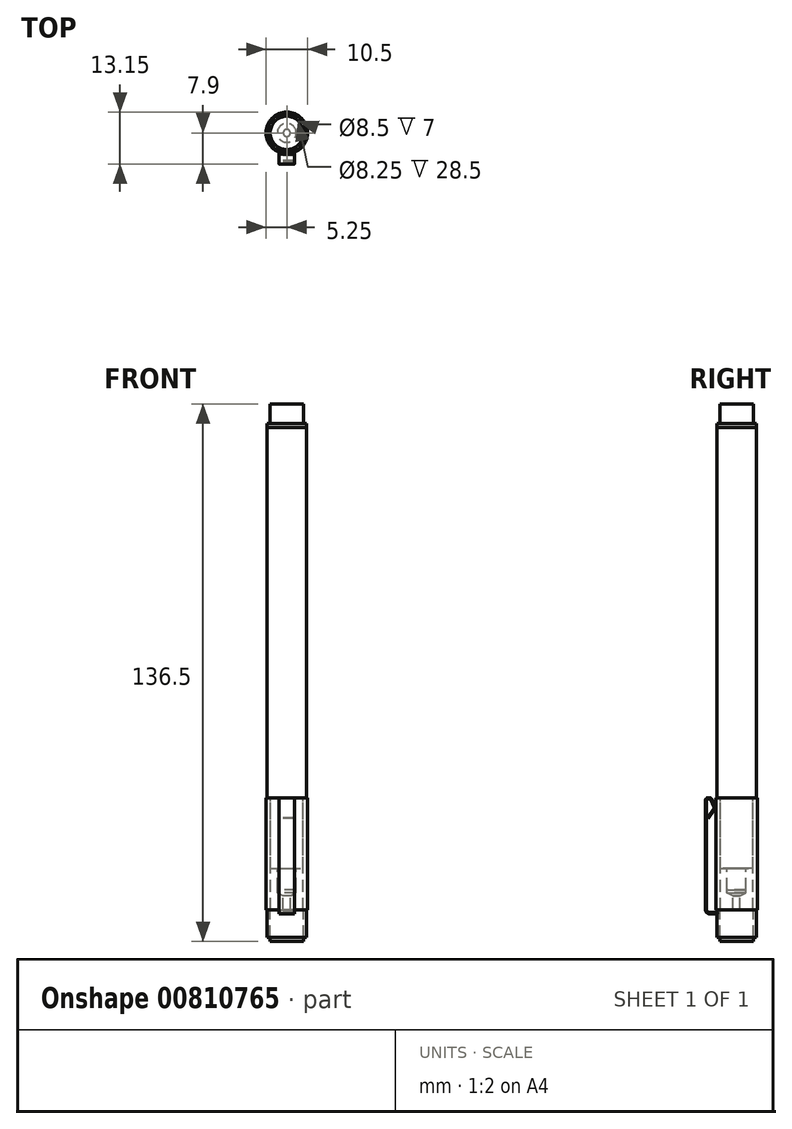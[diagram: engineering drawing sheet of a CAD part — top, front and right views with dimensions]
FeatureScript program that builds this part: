
annotation { "Feature Type Name" : "Feature", "Feature Type Description" : "" }
export const myFeature = defineFeature(function(context is Context, id is Id, definition is map)
    precondition{}
    {
        {
            var Q0;
            Q0=qCreatedBy(makeId("Top.planeOp"),FACE);
            var sketch = newSketch(context, id + "F0", { "sketchPlane" : qUnion([Q0])});
            skCircle(sketch, "E0", {"center": v(0, 0) * mm, "radius": 5 * mm});
            skSolve(sketch);
        }
        {
            var Q0;
            Q0=qSketchRegion(id+"F0",true);
            extrude(context, id + "F1", {"entities" : qUnion([Q0]), "depth" : 94 * mm});
        }
        {
            var Q0;
            Q0=makeQuery(id+"F1.opExtrude","CAP_FACE",FACE,{"disambiguationData":[OSD([sQuery(id+"F0.wireOp",EDGE,"E0")])],"isStart":false});
            var sketch = newSketch(context, id + "F2", { "sketchPlane" : qUnion([Q0])});
            skCircle(sketch, "E1", {"center": v(0, 0) * mm, "radius": 5 * mm});
            skSolve(sketch);
        }
        {
            var Q0;
            Q0=qSketchRegion(id+"F2",true);
            extrude(context, id + "F3", {"entities" : qUnion([Q0]), "depth" : 1 * mm});
        }
        {
            var Q0;
            Q0=makeQuery(id+"F1.opExtrude","CAP_FACE",FACE,{"disambiguationData":[OSD([sQuery(id+"F0.wireOp",EDGE,"E0")])],"isStart":true});
            var sketch = newSketch(context, id + "F4", { "sketchPlane" : qUnion([Q0])});
            skCircle(sketch, "E2", {"center": v(0, 0) * mm, "radius": 4.12 * mm});
            skSolve(sketch);
        }
        {
            var Q0;
            Q0=qSketchRegion(id+"F4",true);
            extrude(context, id + "F5", {"entities" : qUnion([Q0]), "operationType" : NewBodyOperationType.ADD, "depth" : 18 * mm});
        }
        {
            var Q0;
            Q0=makeQuery(id+"F5.opExtrude","CAP_FACE",FACE,{"disambiguationData":[OSD([sQuery(id+"F4.wireOp",EDGE,"E2")])],"isStart":false});
            var sketch = newSketch(context, id + "F6", { "sketchPlane" : qUnion([Q0])});
            skCircle(sketch, "E3", {"center": v(0, 0) * mm, "radius": 2.4 * mm});
            skSolve(sketch);
        }
        {
            var Q0;
            Q0=qSketchRegion(id+"F6",true);
            extrude(context, id + "F7", {"entities" : qUnion([Q0]), "operationType" : NewBodyOperationType.ADD, "depth" : 5.4 * mm});
        }
        {
            var Q0;
            Q0=qCreatedBy(makeId("Front.planeOp"),FACE);
            var sketch = newSketch(context, id + "F8", { "sketchPlane" : qUnion([Q0])});
            skLineSegment(sketch, "E4", {"start": v(2.4, -23.4) * mm, "end": v(2.4, -24.15) * mm});
            skLineSegment(sketch, "E5", {"start": v(2.4, -24.15) * mm, "end": v(0.9, -24.9) * mm});
            skLineSegment(sketch, "E6", {"start": v(0.9, -24.9) * mm, "end": v(0.9, -28.9) * mm});
            skLineSegment(sketch, "E7", {"start": v(0.9, -28.9) * mm, "end": v(0, -28.9) * mm});
            skLineSegment(sketch, "E8", {"start": v(2.4, -23.4) * mm, "end": v(0, -23.4) * mm});
            skLineSegment(sketch, "E9", {"start": v(0, -23.4) * mm, "end": v(0, -28.9) * mm});
            skSolve(sketch);
        }
        {
            var Q0;
            Q0=makeQuery(id+"F8.imprint","IMPRINT",FACE,{"disambiguationData":[TD([[makeQuery(id+"F8.imprint","IMPRINT",EDGE,{"derivedFrom":sQuery(id+"F8.wireOp",EDGE,"E4")}),-1.0]])]});
            var Q1;
            Q1=sQuery(id+"F8.wireOp",EDGE,"E9");
            revolve(context, id + "F9", {"entities" : qUnion([Q0]), "axis" : qUnion([Q1]), "revolveType" : RevolveType.FULL});
        }
        {
            var Q0;
            Q0=makeQuery(id+"F3.opExtrude","CAP_FACE",FACE,{"disambiguationData":[OSD([sQuery(id+"F2.wireOp",EDGE,"E1")])],"isStart":false});
            var sketch = newSketch(context, id + "F10", { "sketchPlane" : qUnion([Q0])});
            skCircle(sketch, "E10", {"center": v(0, 0) * mm, "radius": 4.25 * mm});
            skSolve(sketch);
        }
        {
            var Q0;
            Q0=qSketchRegion(id+"F10",true);
            extrude(context, id + "F11", {"entities" : qUnion([Q0]), "operationType" : NewBodyOperationType.ADD, "depth" : 5 * mm});
        }
        {
            var Q0;
            Q0=qCreatedBy(makeId("Front.planeOp"),FACE);
            var sketch = newSketch(context, id + "F12", { "sketchPlane" : qUnion([Q0])});
            skLineSegment(sketch, "E11", {"start": v(0, -28.9) * mm, "end": v(0.6, -28.9) * mm});
            skLineSegment(sketch, "E12", {"start": v(0.6, -28.9) * mm, "end": v(0.6, -30.31) * mm});
            skLineSegment(sketch, "E13", {"start": v(0.6, -30.31) * mm, "end": v(0, -30.5) * mm});
            skLineSegment(sketch, "E14", {"start": v(0, -30.5) * mm, "end": v(0, -28.9) * mm});
            skSolve(sketch);
        }
        {
            var Q0;
            Q0=makeQuery(id+"F12.imprint","IMPRINT",FACE,{"disambiguationData":[TD([[makeQuery(id+"F12.imprint","IMPRINT",EDGE,{"derivedFrom":sQuery(id+"F12.wireOp",EDGE,"E11")}),-1.0]])]});
            var Q1;
            Q1=sQuery(id+"F12.wireOp",EDGE,"E14");
            revolve(context, id + "F13", {"entities" : qUnion([Q0]), "axis" : qUnion([Q1]), "revolveType" : RevolveType.FULL});
        }
        {
            var Q0;
            Q0=makeQuery(id+"F1.opExtrude","CAP_FACE",FACE,{"disambiguationData":[OSD([sQuery(id+"F0.wireOp",EDGE,"E0")])],"isStart":true});
            var sketch = newSketch(context, id + "F14", { "sketchPlane" : qUnion([Q0])});
            skCircle(sketch, "E15", {"center": v(0, 0) * mm, "radius": 5.25 * mm});
            skCircle(sketch, "E16.0", {"center": v(0, 0) * mm, "radius": 4.12 * mm});
            skSolve(sketch);
        }
        {
            var Q0;
            Q0=qSketchRegion(id+"F14",true);
            extrude(context, id + "F15", {"entities" : qUnion([Q0]), "depth" : 28.5 * mm});
        }
        {
            var Q0;
            Q0=makeQuery(id+"F15.opExtrude","CAP_FACE",FACE,{"disambiguationData":[OSD([sQuery(id+"F14.wireOp",EDGE,"E15"),sQuery(id+"F14.wireOp",EDGE,"E16.0")])],"isStart":false});
            var sketch = newSketch(context, id + "F16", { "sketchPlane" : qUnion([Q0])});
            skCircle(sketch, "E17", {"center": v(0, 0) * mm, "radius": 4.25 * mm});
            skSolve(sketch);
        }
        {
            var Q0;
            Q0=qSketchRegion(id+"F16",true);
            extrude(context, id + "F17", {"entities" : qUnion([Q0]), "operationType" : NewBodyOperationType.ADD, "depth" : (36.5 - 28.5) * mm});
        }
        {
            var Q0;
            Q0=makeQuery(id+"F15.opExtrude","CAP_FACE",FACE,{"disambiguationData":[OSD([sQuery(id+"F14.wireOp",EDGE,"E15"),sQuery(id+"F14.wireOp",EDGE,"E16.0")])],"isStart":false});
            var sketch = newSketch(context, id + "F18", { "sketchPlane" : qUnion([Q0])});
            skCircle(sketch, "E18.0", {"center": v(0, 0) * mm, "radius": 4.25 * mm});
            skCircle(sketch, "E19", {"center": v(0, 0) * mm, "radius": 5 * mm});
            skSolve(sketch);
        }
        {
            var Q0;
            Q0=qSketchRegion(id+"F18",true);
            extrude(context, id + "F19", {"entities" : qUnion([Q0]), "depth" : 7 * mm});
        }
        {
            var Q0;
            Q0=qCreatedBy(makeId("Right.planeOp"),FACE);
            var sketch = newSketch(context, id + "F20", { "sketchPlane" : qUnion([Q0])});
            skLineSegment(sketch, "E20", {"start": v(-7.08, -5.3) * mm, "end": v(-5.54, -2.89) * mm});
            skLineSegment(sketch, "E21", {"start": v(-5.5, -2.24) * mm, "end": v(-6.27, -0.42) * mm});
            skLineSegment(sketch, "E22", {"start": v(-6.91, 0) * mm, "end": v(-7.2, 0) * mm});
            skLineSegment(sketch, "E23", {"start": v(-7.9, -0.7) * mm, "end": v(-7.9, -28.5) * mm});
            skLineSegment(sketch, "E24", {"start": v(-6.9, -29.5) * mm, "end": v(-4.8, -29.5) * mm});
            skPoint(sketch, "E25.visualSharp", {"position": v(-7.9, 0) * mm});
            skArc(sketch, "E25.filletArc", {"start": v(-7.2, 0) * mm, "mid": v(-7.7, -0.2) * mm, "end": v(-7.9, -0.7) * mm});
            skPoint(sketch, "E26.visualSharp", {"position": v(-6.45, 0) * mm});
            skArc(sketch, "E26.filletArc", {"start": v(-6.27, -0.42) * mm, "mid": v(-6.53, -0.12) * mm, "end": v(-6.91, 0) * mm});
            skPoint(sketch, "E27.visualSharp", {"position": v(-5.34, -2.58) * mm});
            skArc(sketch, "E27.filletArc", {"start": v(-5.54, -2.89) * mm, "mid": v(-5.44, -2.57) * mm, "end": v(-5.5, -2.24) * mm});
            skPoint(sketch, "E28.visualSharp", {"position": v(-7.9, -29.5) * mm});
            skArc(sketch, "E28.filletArc", {"start": v(-7.9, -28.5) * mm, "mid": v(-7.6, -29.2) * mm, "end": v(-6.9, -29.5) * mm});
            skLineSegment(sketch, "E29.0", {"start": v(-6.9, -29.2) * mm, "end": v(-4.8, -29.2) * mm});
            skArc(sketch, "E29.1", {"start": v(-7.6, -28.5) * mm, "mid": v(-7.4, -29) * mm, "end": v(-6.9, -29.2) * mm});
            skLineSegment(sketch, "E29.2", {"start": v(-7.6, -0.7) * mm, "end": v(-7.6, -28.5) * mm});
            skArc(sketch, "E29.3", {"start": v(-7.2, -0.3) * mm, "mid": v(-7.48, -0.42) * mm, "end": v(-7.6, -0.7) * mm});
            skLineSegment(sketch, "E29.4", {"start": v(-6.91, -0.3) * mm, "end": v(-7.2, -0.3) * mm});
            skLineSegment(sketch, "E29.5", {"start": v(-7.33, -5.13) * mm, "end": v(-5.8, -2.73) * mm});
            skArc(sketch, "E29.6", {"start": v(-5.8, -2.73) * mm, "mid": v(-5.73, -2.55) * mm, "end": v(-5.77, -2.35) * mm});
            skLineSegment(sketch, "E29.7", {"start": v(-5.77, -2.35) * mm, "end": v(-6.55, -0.54) * mm});
            skArc(sketch, "E29.8", {"start": v(-6.55, -0.54) * mm, "mid": v(-6.7, -0.37) * mm, "end": v(-6.91, -0.3) * mm});
            skLineSegment(sketch, "E30", {"start": v(-7.33, -5.13) * mm, "end": v(-7.08, -5.3) * mm});
            skLineSegment(sketch, "E31", {"start": v(-4.8, -29.2) * mm, "end": v(-4.8, -29.5) * mm});
            skSolve(sketch);
        }
        {
            var Q0;
            Q0=qSketchRegion(id+"F20",true);
            extrude(context, id + "F21", {"entities" : qUnion([Q0]), "operationType" : NewBodyOperationType.ADD, "depth" : 4 * mm, "symmetric" : true});
        }
    });
